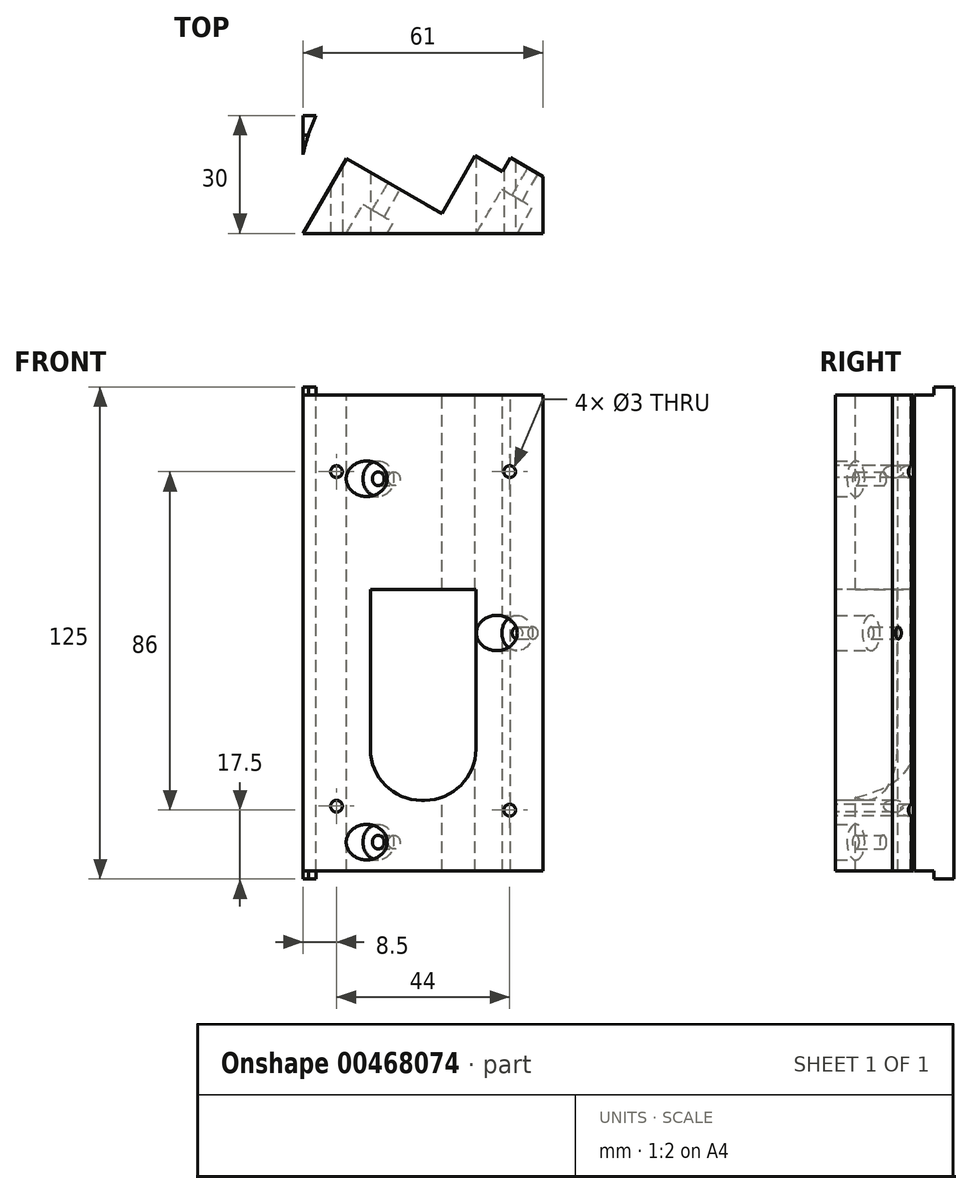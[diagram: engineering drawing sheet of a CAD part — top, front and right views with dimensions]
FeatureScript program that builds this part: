
annotation { "Feature Type Name" : "Feature", "Feature Type Description" : "" }
export const myFeature = defineFeature(function(context is Context, id is Id, definition is map)
    precondition{}
    {
        {
            var Q0;
            Q0=qCreatedBy(makeId("Front.planeOp"),FACE);
            var sketch = newSketch(context, id + "F0", { "sketchPlane" : qUnion([Q0])});
            skLineSegment(sketch, "E0.bottom", {"start": v(30.5, -62.5) * mm, "end": v(-30.5, -62.5) * mm});
            skLineSegment(sketch, "E0.top", {"start": v(30.5, 62.5) * mm, "end": v(-30.5, 62.5) * mm});
            skLineSegment(sketch, "E0.left", {"start": v(30.5, -62.5) * mm, "end": v(30.5, 62.5) * mm});
            skLineSegment(sketch, "E0.right", {"start": v(-30.5, -62.5) * mm, "end": v(-30.5, 62.5) * mm});
            skPoint(sketch, "E0.middle", {"position": v(0, 0) * mm});
            skCircle(sketch, "E1", {"center": v(-22, 41) * mm, "radius": 1.5 * mm});
            skCircle(sketch, "E2", {"center": v(22, 41) * mm, "radius": 1.5 * mm});
            skCircle(sketch, "E3", {"center": v(22, -45) * mm, "radius": 1.5 * mm});
            skCircle(sketch, "E4", {"center": v(-22, -44) * mm, "radius": 1.5 * mm});
            skSolve(sketch);
        }
        {
            var Q0;
            Q0 = qSketchRegion(id + "F0", true);
            extrude(context, id + "F1", {"entities" : qUnion([Q0]), "oppositeDirection" : true, "depth" : 30 * mm});
        }
        {
            var Q0;
            Q0=makeQuery(id+"F1.opExtrude","CAP_FACE",FACE,{"disambiguationData":[OSD([sQuery(id+"F0.wireOp",EDGE,"E0.bottom"),sQuery(id+"F0.wireOp",EDGE,"E0.top"),sQuery(id+"F0.wireOp",EDGE,"E0.left"),sQuery(id+"F0.wireOp",EDGE,"E0.right"),sQuery(id+"F0.wireOp",EDGE,"E1"),sQuery(id+"F0.wireOp",EDGE,"E2"),sQuery(id+"F0.wireOp",EDGE,"E3"),sQuery(id+"F0.wireOp",EDGE,"E4")])],"isStart":true});
            var sketch = newSketch(context, id + "F2", { "sketchPlane" : qUnion([Q0])});
            skLineSegment(sketch, "E5.bottom", {"start": v(13.4, -42.5) * mm, "end": v(-13.4, -42.5) * mm});
            skLineSegment(sketch, "E5.top", {"start": v(13.4, 11) * mm, "end": v(-13.4, 11) * mm});
            skLineSegment(sketch, "E5.left", {"start": v(13.4, -42.5) * mm, "end": v(13.4, 11) * mm});
            skLineSegment(sketch, "E5.right", {"start": v(-13.4, -42.5) * mm, "end": v(-13.4, 11) * mm});
            skPoint(sketch, "E5.middle", {"position": v(0, -15.75) * mm});
            skSolve(sketch);
        }
        {
            var Q0;
            Q0 = qSketchRegion(id + "F2", true);
            extrude(context, id + "F3", {"entities" : qUnion([Q0]), "operationType" : NewBodyOperationType.REMOVE, "oppositeDirection" : true, "depth" : 100 * mm});
        }
        {
            var Q0;
            Q0=makeQuery(id+"F3.boolean.opBoolean","COPY",EDGE,{"derivedFrom":makeQuery(id+"F3.opExtrude","SWEPT_EDGE",EDGE,{"disambiguationData":[OSD([sQuery(id+"F2.wireOp",EDGE,"E5.bottom"),sQuery(id+"F2.wireOp",EDGE,"E5.right")])]})});
            var Q1;
            Q1=makeQuery(id+"F3.boolean.opBoolean","COPY",EDGE,{"derivedFrom":makeQuery(id+"F3.opExtrude","SWEPT_EDGE",EDGE,{"disambiguationData":[OSD([sQuery(id+"F2.wireOp",EDGE,"E5.bottom"),sQuery(id+"F2.wireOp",EDGE,"E5.left")])]})});
            fillet(context, id + "F4", {"entities" : qUnion([Q0, Q1]), "radius" : 13 * mm, "tangentPropagation" : true, "allowEdgeOverflow" : false});
        }
        {
            var Q0;
            Q0=makeQuery(id+"F1.opExtrude","SWEPT_FACE",FACE,{"disambiguationData":[OSD([sQuery(id+"F0.wireOp",EDGE,"E0.top")])]});
            var sketch = newSketch(context, id + "F5", { "sketchPlane" : qUnion([Q0])});
            skLineSegment(sketch, "E6", {"start": v(-30.5, 0) * mm, "end": v(-19.5, 19.05) * mm});
            skLineSegment(sketch, "E7", {"start": v(-19.5, 19.05) * mm, "end": v(4.75, 5.05) * mm});
            skLineSegment(sketch, "E8", {"start": v(4.75, 5.05) * mm, "end": v(13.25, 19.77) * mm});
            skLineSegment(sketch, "E9", {"start": v(13.25, 19.77) * mm, "end": v(20.18, 15.77) * mm});
            skLineSegment(sketch, "E10", {"start": v(20.18, 15.77) * mm, "end": v(22.18, 19.24) * mm});
            skLineSegment(sketch, "E11", {"start": v(22.18, 19.24) * mm, "end": v(39.5, 9.24) * mm});
            skLineSegment(sketch, "E12", {"start": v(39.5, 9.24) * mm, "end": v(55.58, 37.1) * mm});
            skArc(sketch, "E13", {"start": v(55.58, 37.1) * mm, "mid": v(-2.7, 53.9) * mm, "end": v(-30.5, 0) * mm});
            skSolve(sketch);
        }
        {
            var Q0;
            Q0 = qSketchRegion(id + "F5", true);
            extrude(context, id + "F6", {"entities" : qUnion([Q0]), "operationType" : NewBodyOperationType.REMOVE, "oppositeDirection" : true, "depth" : 146.1 * mm});
        }
        {
            var Q0;
            Q0=makeQuery(id+"F6.boolean.opBoolean","COPY",FACE,{"derivedFrom":makeQuery(id+"F6.opExtrude","SWEPT_FACE",FACE,{"disambiguationData":[OSD([sQuery(id+"F5.wireOp",EDGE,"E7")])]})});
            var sketch = newSketch(context, id + "F7", { "sketchPlane" : qUnion([Q0])});
            skCircle(sketch, "E14", {"center": v(12.41, 39.18) * mm, "radius": 1.75 * mm});
            skPoint(sketch, "E14.centerSnap0", {"position": v(12.41, 62.5) * mm});
            skPoint(sketch, "E14.perimeterSnap0", {"position": v(12.41, 62.5) * mm});
            skPoint(sketch, "E14.perimeterSnap1", {"position": v(-1.59, 36.75) * mm});
            skCircle(sketch, "E15", {"center": v(12.41, -53.14) * mm, "radius": 1.75 * mm});
            skPoint(sketch, "E15.centerSnap0", {"position": v(12.41, -62.5) * mm});
            skSolve(sketch);
        }
        {
            var Q0;
            Q0 = qSketchRegion(id + "F7", true);
            extrude(context, id + "F8", {"entities" : qUnion([Q0]), "operationType" : NewBodyOperationType.REMOVE, "oppositeDirection" : true, "depth" : 100 * mm});
        }
        {
            var Q0;
            Q0=makeQuery(id+"F6.boolean.opBoolean","COPY",FACE,{"derivedFrom":makeQuery(id+"F6.opExtrude","SWEPT_FACE",FACE,{"disambiguationData":[OSD([sQuery(id+"F5.wireOp",EDGE,"E7")])]})});
            var sketch = newSketch(context, id + "F9", { "sketchPlane" : qUnion([Q0])});
            skCircle(sketch, "E16", {"center": v(12.41, 39.18) * mm, "radius": 4.5 * mm});
            skCircle(sketch, "E17", {"center": v(12.41, -53.14) * mm, "radius": 4.5 * mm});
            skSolve(sketch);
        }
        {
            var Q0;
            Q0 = qSketchRegion(id + "F9", true);
            extrude(context, id + "F10", {"entities" : qUnion([Q0]), "operationType" : NewBodyOperationType.REMOVE, "oppositeDirection" : true, "depth" : 110 * mm, "hasSecondDirection" : true, "secondDirectionOppositeDirection" : true, "secondDirectionDepth" : 8 * mm});
        }
        {
            var Q0;
            Q0=makeQuery(id+"F6.boolean.opBoolean","COPY",FACE,{"derivedFrom":makeQuery(id+"F6.opExtrude","SWEPT_FACE",FACE,{"disambiguationData":[OSD([sQuery(id+"F5.wireOp",EDGE,"E9")])]})});
            var sketch = newSketch(context, id + "F11", { "sketchPlane" : qUnion([Q0])});
            skCircle(sketch, "E18", {"center": v(-16.22, 0) * mm, "radius": 1.5 * mm});
            skPoint(sketch, "E18.centerSnap0", {"position": v(-9.59, 0) * mm});
            skSolve(sketch);
        }
        {
            var Q0;
            Q0 = qSketchRegion(id + "F11", true);
            extrude(context, id + "F12", {"entities" : qUnion([Q0]), "operationType" : NewBodyOperationType.REMOVE, "endBound" : BoundingType.SYMMETRIC, "oppositeDirection" : true, "depth" : 82.4 * mm});
        }
        {
            var Q0;
            Q0=makeQuery(id+"F6.boolean.opBoolean","COPY",FACE,{"derivedFrom":makeQuery(id+"F6.opExtrude","SWEPT_FACE",FACE,{"disambiguationData":[OSD([sQuery(id+"F5.wireOp",EDGE,"E11")])]})});
            var sketch = newSketch(context, id + "F13", { "sketchPlane" : qUnion([Q0])});
            skCircle(sketch, "E19", {"center": v(-16.22, 0) * mm, "radius": 4.5 * mm});
            skSolve(sketch);
        }
        {
            var Q0;
            Q0 = qSketchRegion(id + "F13", true);
            extrude(context, id + "F14", {"entities" : qUnion([Q0]), "operationType" : NewBodyOperationType.REMOVE, "oppositeDirection" : true, "depth" : 44.8 * mm, "hasSecondDirection" : true, "secondDirectionOppositeDirection" : true, "secondDirectionDepth" : 8 * mm});
        }
        {
            var Q0;
            Q0=makeQuery(id+"F1.opExtrude","CAP_FACE",FACE,{"disambiguationData":[OSD([sQuery(id+"F0.wireOp",EDGE,"E0.bottom"),sQuery(id+"F0.wireOp",EDGE,"E0.top"),sQuery(id+"F0.wireOp",EDGE,"E0.left"),sQuery(id+"F0.wireOp",EDGE,"E0.right"),sQuery(id+"F0.wireOp",EDGE,"E1"),sQuery(id+"F0.wireOp",EDGE,"E2"),sQuery(id+"F0.wireOp",EDGE,"E3"),sQuery(id+"F0.wireOp",EDGE,"E4")])],"isStart":true});
            var sketch = newSketch(context, id + "F15", { "sketchPlane" : qUnion([Q0])});
            skLineSegment(sketch, "E20.bottom", {"start": v(-30.5, 60.5) * mm, "end": v(30.5, 60.5) * mm});
            skLineSegment(sketch, "E20.top", {"start": v(-30.5, 62.5) * mm, "end": v(30.5, 62.5) * mm});
            skLineSegment(sketch, "E20.left", {"start": v(-30.5, 60.5) * mm, "end": v(-30.5, 62.5) * mm});
            skLineSegment(sketch, "E20.right", {"start": v(30.5, 60.5) * mm, "end": v(30.5, 62.5) * mm});
            skLineSegment(sketch, "E21.bottom", {"start": v(-30.5, -62.5) * mm, "end": v(30.5, -62.5) * mm});
            skLineSegment(sketch, "E21.top", {"start": v(-30.5, -60.5) * mm, "end": v(30.5, -60.5) * mm});
            skLineSegment(sketch, "E21.left", {"start": v(-30.5, -62.5) * mm, "end": v(-30.5, -60.5) * mm});
            skLineSegment(sketch, "E21.right", {"start": v(30.5, -62.5) * mm, "end": v(30.5, -60.5) * mm});
            skSolve(sketch);
        }
        {
            var Q0;
            Q0 = qSketchRegion(id + "F15", true);
            extrude(context, id + "F16", {"entities" : qUnion([Q0]), "operationType" : NewBodyOperationType.REMOVE, "oppositeDirection" : true, "depth" : 25 * mm});
        }
    });
